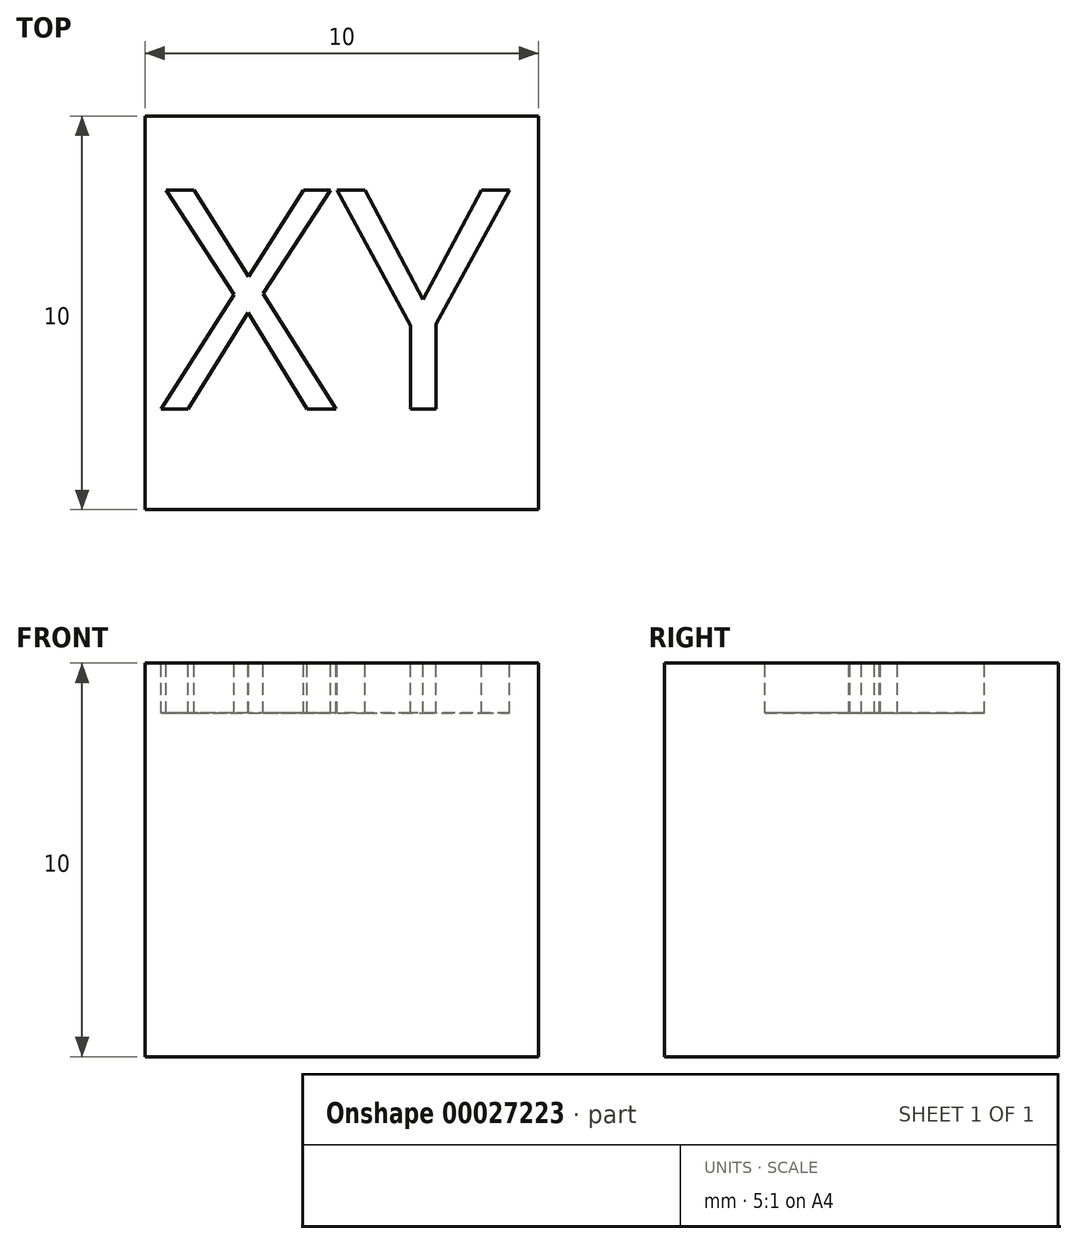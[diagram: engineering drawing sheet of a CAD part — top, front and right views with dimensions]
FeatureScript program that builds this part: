
annotation { "Feature Type Name" : "Feature", "Feature Type Description" : "" }
export const myFeature = defineFeature(function(context is Context, id is Id, definition is map)
    precondition{}
    {
        {
            var Q0;
            Q0=qCreatedBy(makeId("Top.planeOp"),FACE);
            var sketch = newSketch(context, id + "F0", { "sketchPlane" : qUnion([Q0])});
            skLineSegment(sketch, "E0.bottom", {"start": v(0, 0) * mm, "end": v(10, 0) * mm});
            skLineSegment(sketch, "E0.top", {"start": v(0, -10) * mm, "end": v(10, -10) * mm});
            skLineSegment(sketch, "E0.left", {"start": v(0, 0) * mm, "end": v(0, -10) * mm});
            skLineSegment(sketch, "E0.right", {"start": v(10, 0) * mm, "end": v(10, -10) * mm});
            skSolve(sketch);
        }
        {
            var Q0;
            Q0=qCreatedBy(makeId("Front.planeOp"),FACE);
            var sketch = newSketch(context, id + "F1", { "sketchPlane" : qUnion([Q0])});
            skLineSegment(sketch, "E1.0", {"start": v(0, 0) * mm, "end": v(10, 0) * mm});
            skLineSegment(sketch, "E2", {"start": v(0, 0) * mm, "end": v(0, 10) * mm});
            skLineSegment(sketch, "E3", {"start": v(0, 10) * mm, "end": v(10, 10) * mm});
            skLineSegment(sketch, "E4", {"start": v(10, 10) * mm, "end": v(10, 0) * mm});
            skSolve(sketch);
        }
        {
            var Q0;
            Q0=sQuery(id+"F0.wireOp",VERTEX,"E0.left.end");
            var Q1;
            Q1=qCreatedBy(makeId("Front.planeOp"),FACE);
            cPlane(context, id + "F2", {"entities" : qUnion([Q0, Q1]), "cplaneType" : CPlaneType.PLANE_POINT, "offset" : 150 * mm, "width" : 150 * mm, "height" : 150 * mm});
        }
        {
            var Q0;
            Q0=makeQuery(id+"F1.imprint","IMPRINT",FACE,{"disambiguationData":[TD([[makeQuery(id+"F1.imprint","IMPRINT",EDGE,{"derivedFrom":sQuery(id+"F1.wireOp",EDGE,"E1.0")}),1.0]])]});
            var Q1;
            Q1=qCreatedBy(id+"F2.planeOp",FACE);
            extrude(context, id + "F3", {"entities" : qUnion([Q0]), "endBound" : BoundingType.UP_TO_SURFACE, "endBoundEntityFace" : qUnion([Q1]), "depth" : 25 * mm});
        }
        {
            var Q0;
            Q0=makeQuery(id+"F3.opExtrude","SWEPT_FACE",FACE,{"disambiguationData":[OSD([sQuery(id+"F1.wireOp",EDGE,"E3")])]});
            var sketch = newSketch(context, id + "F4", { "sketchPlane" : qUnion([Q0])});
            skText(sketch, "E5", { "text": "XY", "fontName": "OpenSans-Regular.ttf"});
            const initialGuessF4  = {"E5": [0.00038, -0.00745, 1, 0, 0.00562]};
            skSetInitialGuess(sketch, initialGuessF4);
            skSolve(sketch);
        }
        {
            var Q0;
            Q0=makeQuery(id+"F4.imprint","IMPRINT",FACE,{"disambiguationData":[TD([[makeQuery(id+"F4.imprint","IMPRINT",EDGE,{"derivedFrom":sQuery(id+"F4.wireOp",EDGE,"E5.sketch_text.stroke-0")}),-1.0]])]});
            var Q1;
            Q1=makeQuery(id+"F4.imprint","IMPRINT",FACE,{"disambiguationData":[TD([[makeQuery(id+"F4.imprint","IMPRINT",EDGE,{"derivedFrom":sQuery(id+"F4.wireOp",EDGE,"E5.sketch_text.stroke-12")}),-1.0]])]});
            extrude(context, id + "F5", {"entities" : qUnion([Q0, Q1]), "operationType" : NewBodyOperationType.REMOVE, "oppositeDirection" : true, "depth" : 1.27 * mm, "offsetDistance" : 25.4 * mm});
        }
    });
